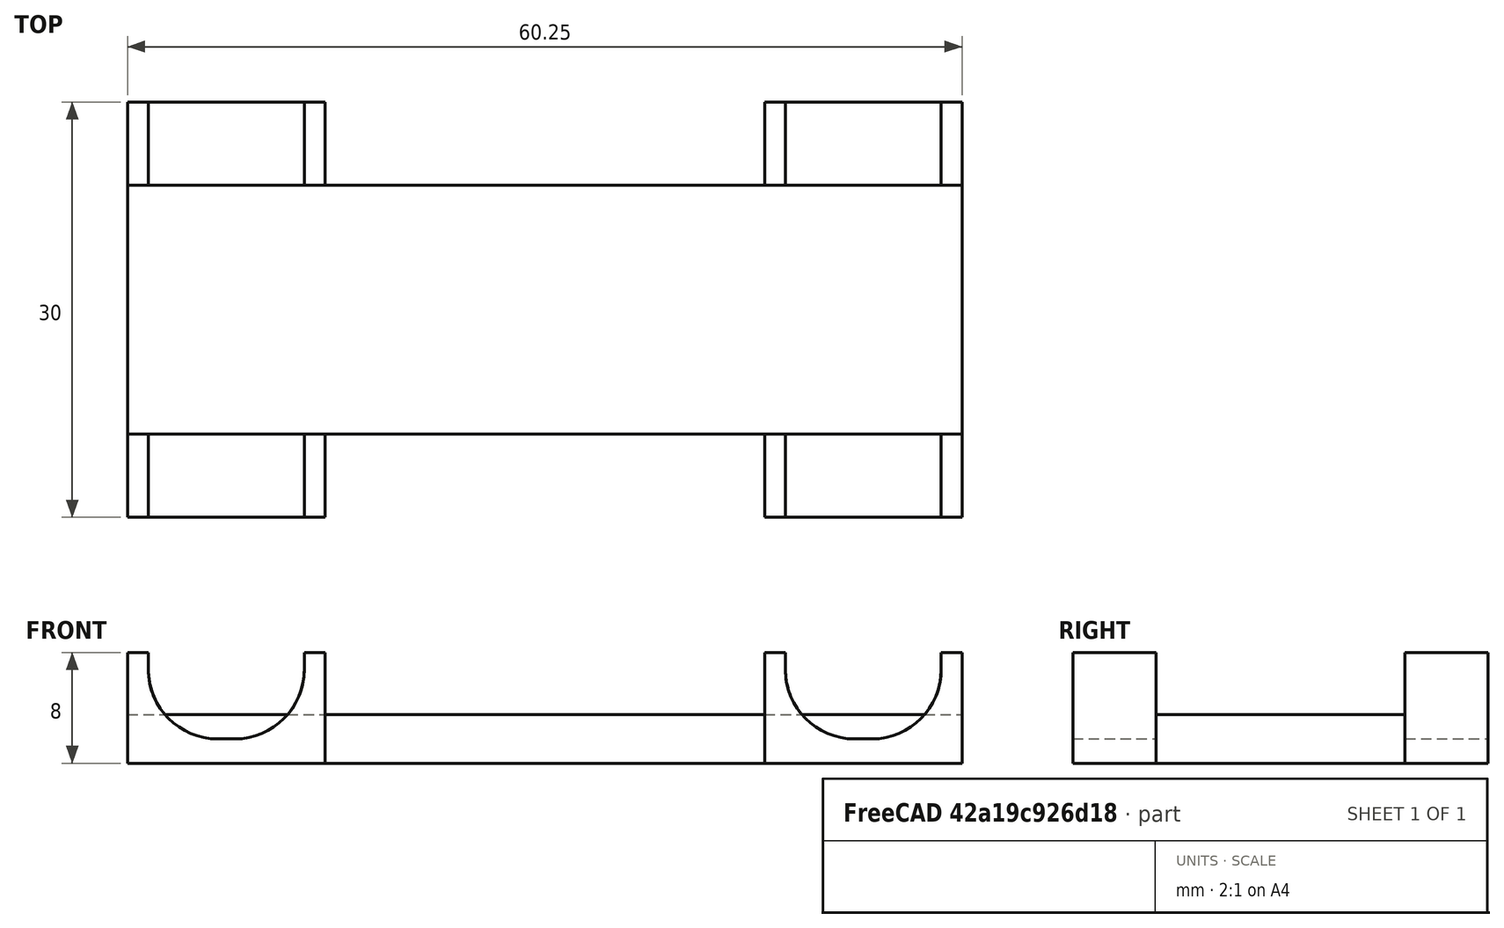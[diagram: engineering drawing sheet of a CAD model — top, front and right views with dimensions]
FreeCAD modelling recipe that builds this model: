
FCSTD DOCUMENT  (FreeCAD 0.19R24276 (Git))
Label: axleJig2
License: All rights reserved
LicenseURL: http://en.wikipedia.org/wiki/All_rights_reserved
objects: Part::Box×9, Part::Cut×4, Part::Fillet×4, Part::MultiFuse×2, Spreadsheet::Sheet×1
note: 19 computed .brp shape members not serialized (recipe doc carries the construction recipe); baked Part::Feature solids carry a one-line shape summary decoded from their .brp

FEATURE [Part::Box] Box  label="Cube"
  AttacherType = Attacher::AttachEngine3D
  Height = 8
  Length = 14.25
  Width = 6
  expr: Width = <<data>>.wheel_width
  expr: Length = <<data>>.wheel_diameter + 2 * <<data>>.post_thickness
FEATURE [Part::Box] Box001  label="Cube001"
  AttacherType = Attacher::AttachEngine3D
  Height = 10
  Length = 11.25
  Placement = pos=(1.5,0,1.75) rot=(0,0,1;0rad)
  Width = 6
  expr: Width = <<data>>.wheel_width
  expr: .Placement.Base.z = <<data>>.ride_height
  expr: .Placement.Base.x = <<data>>.post_thickness
  expr: Length = <<data>>.wheel_diameter
FEATURE [Part::Cut] Cut  label="wheel01"
  Base = -> Box
  Tool = -> Box001
FEATURE [Part::Box] Box008  label="Cube008"
  AttacherType = Attacher::AttachEngine3D
  Height = 3.5
  Length = 60.25
  Placement = pos=(0,6,0) rot=(0,0,1;0rad)
  Width = 18
  expr: .Placement.Base.y = <<data>>.wheel_width
  expr: Height = <<data>>.ride_height * 2
  expr: Width = <<data>>.axle_width
  expr: Length = <<data>>.wheel_diameter + 2 * <<data>>.post_thickness + <<data>>.wheel_base
FEATURE [Spreadsheet::Sheet] Spreadsheet  label="data"
  cells = A4=wheel_base; B4(wheel_base)==46mm; A5=axle_width; B5(axle_width)==18mm; A6=ride_height; B6(ride_height)==1.75mm; A7=axle_diameter; B7(axle_diameter)==1.75mm; A8=post_wdith; B8(post_wdith)==10mm; A9=post_thickness; B9(post_thickness)==1.5mm; A10=wheel_diameter; B10(wheel_diameter)==11.25mm; A11=wheel_width; B11(wheel_width)==6mm
FEATURE [Part::Box] Box009  label="Cube009"
  AttacherType = Attacher::AttachEngine3D
  Height = 8
  Length = 14.25
  Width = 6
  expr: Width = <<data>>.wheel_width
  expr: Length = <<data>>.wheel_diameter + 2 * <<data>>.post_thickness
FEATURE [Part::Box] Box010  label="Cube010"
  AttacherType = Attacher::AttachEngine3D
  Height = 10
  Length = 11.25
  Placement = pos=(1.5,0,1.75) rot=(0,0,1;0rad)
  Width = 6
  expr: Width = <<data>>.wheel_width
  expr: .Placement.Base.z = <<data>>.ride_height
  expr: Length = <<data>>.wheel_diameter
  expr: .Placement.Base.x = <<data>>.post_thickness
FEATURE [Part::Cut] Cut001  label="wheel002"
  Base = -> Box009
  Placement = pos=(0,24,0) rot=(0,0,1;0rad)
  Tool = -> Box010
  expr: .Placement.Base.y = <<data>>.axle_width + <<data>>.wheel_width
FEATURE [Part::Fillet] Fillet
  Base = -> Cut
  Edges = 2 edges r=5: [Edge23,Edge24]
FEATURE [Part::Fillet] Fillet001
  Base = -> Cut001
  Edges = 2 edges r=5: [Edge23,Edge24]
FEATURE [Part::MultiFuse] Fusion  label="axle01"
  Shapes = -> [Fillet001,Fillet]
FEATURE [Part::Box] Box011  label="Cube011"
  AttacherType = Attacher::AttachEngine3D
  Height = 8
  Length = 14.25
  Width = 6
  expr: Length = <<data>>.wheel_diameter + 2 * <<data>>.post_thickness
  expr: Width = <<data>>.wheel_width
FEATURE [Part::Box] Box012  label="Cube012"
  AttacherType = Attacher::AttachEngine3D
  Height = 10
  Length = 11.25
  Placement = pos=(1.5,0,1.75) rot=(0,0,1;0rad)
  Width = 6
  expr: Length = <<data>>.wheel_diameter
  expr: .Placement.Base.x = <<data>>.post_thickness
  expr: .Placement.Base.z = <<data>>.ride_height
  expr: Width = <<data>>.wheel_width
FEATURE [Part::Box] Box013  label="Cube013"
  AttacherType = Attacher::AttachEngine3D
  Height = 8
  Length = 14.25
  Width = 6
  expr: Length = <<data>>.wheel_diameter + 2 * <<data>>.post_thickness
  expr: Width = <<data>>.wheel_width
FEATURE [Part::Box] Box014  label="Cube014"
  AttacherType = Attacher::AttachEngine3D
  Height = 10
  Length = 11.25
  Placement = pos=(1.5,0,1.75) rot=(0,0,1;0rad)
  Width = 6
  expr: .Placement.Base.x = <<data>>.post_thickness
  expr: Length = <<data>>.wheel_diameter
  expr: .Placement.Base.z = <<data>>.ride_height
  expr: Width = <<data>>.wheel_width
FEATURE [Part::Cut] Cut002  label="wheel003"
  Base = -> Box013
  Placement = pos=(0,24,0) rot=(0,0,1;0rad)
  Tool = -> Box014
  expr: .Placement.Base.y = <<data>>.axle_width + <<data>>.wheel_width
FEATURE [Part::Fillet] Fillet002
  Base = -> Cut002
  Edges = 2 edges r=5: [Edge23,Edge24]
FEATURE [Part::Cut] Cut003  label="wheel004"
  Base = -> Box011
  Tool = -> Box012
FEATURE [Part::Fillet] Fillet003
  Base = -> Cut003
  Edges = 2 edges r=5: [Edge23,Edge24]
FEATURE [Part::MultiFuse] Fusion001  label="axle02"
  Placement = pos=(46,0,0) rot=(0,0,1;0rad)
  Shapes = -> [Fillet002,Fillet003]
  expr: .Placement.Base.x = <<data>>.wheel_base
